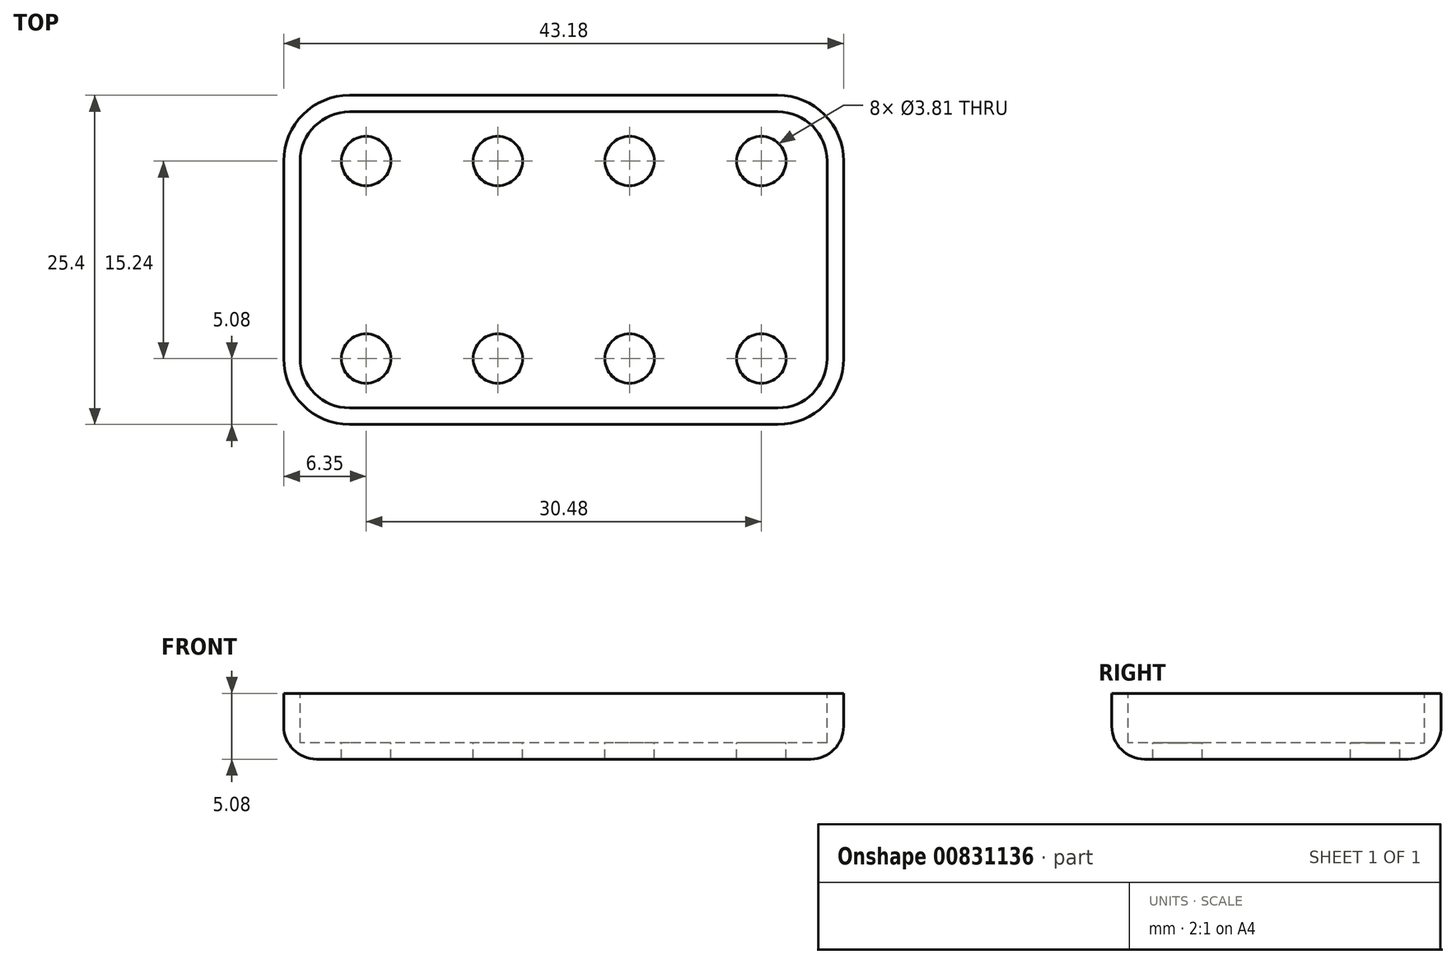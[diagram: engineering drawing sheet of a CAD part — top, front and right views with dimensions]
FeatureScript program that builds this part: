
annotation { "Feature Type Name" : "Feature", "Feature Type Description" : "" }
export const myFeature = defineFeature(function(context is Context, id is Id, definition is map)
    precondition{}
    {
        {
            var Q0;
            Q0=qCreatedBy(makeId("Top.planeOp"),FACE);
            var sketch = newSketch(context, id + "F0", { "sketchPlane" : qUnion([Q0])});
            skLineSegment(sketch, "E0.bottom", {"start": v(-22.86, 12.7) * mm, "end": v(22.86, 12.7) * mm});
            skLineSegment(sketch, "E0.top", {"start": v(-22.86, -12.7) * mm, "end": v(22.86, -12.7) * mm});
            skLineSegment(sketch, "E0.left", {"start": v(-22.86, 12.7) * mm, "end": v(-22.86, -12.7) * mm});
            skLineSegment(sketch, "E0.right", {"start": v(22.86, 12.7) * mm, "end": v(22.86, -12.7) * mm});
            skSolve(sketch);
        }
        {
            var Q0;
            Q0=qCreatedBy(makeId("Top.planeOp"),FACE);
            var sketch = newSketch(context, id + "F1", { "sketchPlane" : qUnion([Q0])});
            skLineSegment(sketch, "E1.bottom", {"start": v(16.51, 12.7) * mm, "end": v(-16.5, 12.7) * mm});
            skLineSegment(sketch, "E1.top", {"start": v(16.51, -12.7) * mm, "end": v(-16.5, -12.7) * mm});
            skLineSegment(sketch, "E1.left", {"start": v(21.6, 7.62) * mm, "end": v(21.6, -7.62) * mm});
            skLineSegment(sketch, "E1.right", {"start": v(-21.59, 7.62) * mm, "end": v(-21.59, -7.62) * mm});
            skPoint(sketch, "E1.middle", {"position": v(0, 0) * mm});
            skPoint(sketch, "E2.visualSharp", {"position": v(-21.59, 12.7) * mm});
            skArc(sketch, "E2.filletArc", {"start": v(-16.5, 12.7) * mm, "mid": v(-20.1, 11.21) * mm, "end": v(-21.59, 7.62) * mm});
            skPoint(sketch, "E3.visualSharp", {"position": v(21.59, 12.7) * mm});
            skArc(sketch, "E3.filletArc", {"start": v(21.59, 7.62) * mm, "mid": v(20.1, 11.21) * mm, "end": v(16.51, 12.7) * mm});
            skPoint(sketch, "E4.visualSharp", {"position": v(21.6, -12.7) * mm});
            skArc(sketch, "E4.filletArc", {"start": v(16.51, -12.7) * mm, "mid": v(20.1, -11.21) * mm, "end": v(21.6, -7.62) * mm});
            skPoint(sketch, "E5.visualSharp", {"position": v(-21.59, -12.7) * mm});
            skArc(sketch, "E5.filletArc", {"start": v(-21.59, -7.62) * mm, "mid": v(-20.1, -11.21) * mm, "end": v(-16.5, -12.7) * mm});
            skSolve(sketch);
        }
        {
            var Q0;
            Q0=qCreatedBy(makeId("Top.planeOp"),FACE);
            cPlane(context, id + "F2", {"entities" : qUnion([Q0]), "cplaneType" : CPlaneType.OFFSET, "offset" : 7.62 * mm, "oppositeDirection" : true, "width" : 152.4 * mm, "height" : 152.4 * mm});
        }
        {
            var Q0;
            Q0=qCreatedBy(id+"F2.planeOp",FACE);
            var sketch = newSketch(context, id + "F3", { "sketchPlane" : qUnion([Q0])});
            skCircle(sketch, "E6", {"center": v(15.24, -7.62) * mm, "radius": 1.52 * mm});
            skCircle(sketch, "E7", {"center": v(15.24, 7.62) * mm, "radius": 1.52 * mm});
            skCircle(sketch, "E8.1.0.0", {"center": v(5.08, -7.62) * mm, "radius": 1.52 * mm});
            skCircle(sketch, "E8.2.0.0", {"center": v(-5.08, -7.62) * mm, "radius": 1.52 * mm});
            skCircle(sketch, "E8.3.0.0", {"center": v(-15.24, -7.62) * mm, "radius": 1.52 * mm});
            skLineSegment(sketch, "E8.direction1", {"start": v(15.24, -7.62) * mm, "end": v(5.08, -7.62) * mm, "construction": true});
            skCircle(sketch, "E9.1.0.0", {"center": v(5.08, 7.62) * mm, "radius": 1.52 * mm});
            skCircle(sketch, "E9.2.0.0", {"center": v(-5.08, 7.62) * mm, "radius": 1.52 * mm});
            skCircle(sketch, "E9.3.0.0", {"center": v(-15.24, 7.62) * mm, "radius": 1.52 * mm});
            skLineSegment(sketch, "E9.direction1", {"start": v(15.24, 7.62) * mm, "end": v(5.08, 7.62) * mm, "construction": true});
            skSolve(sketch);
        }
        {
            var Q0;
            Q0=makeQuery(id+"F1.imprint","IMPRINT",FACE,{"disambiguationData":[TD([[makeQuery(id+"F1.imprint","IMPRINT",EDGE,{"derivedFrom":sQuery(id+"F1.wireOp",EDGE,"E1.bottom")}),1.0]])]});
            extrude(context, id + "F4", {"entities" : qUnion([Q0]), "oppositeDirection" : true, "depth" : 5.08 * mm, "offsetDistance" : 25.4 * mm});
        }
        {
            var Q0;
            Q0=makeQuery(id+"F4.opExtrude","CAP_FACE",FACE,{"disambiguationData":[OSD([sQuery(id+"F1.wireOp",EDGE,"E1.bottom"),sQuery(id+"F1.wireOp",EDGE,"E1.top"),sQuery(id+"F1.wireOp",EDGE,"E1.left"),sQuery(id+"F1.wireOp",EDGE,"E1.right"),sQuery(id+"F1.wireOp",EDGE,"E2.filletArc"),sQuery(id+"F1.wireOp",EDGE,"E3.filletArc"),sQuery(id+"F1.wireOp",EDGE,"E4.filletArc"),sQuery(id+"F1.wireOp",EDGE,"E5.filletArc")])],"isStart":true});
            shell(context, id + "F5", {"entities" : qUnion([Q0]), "thickness" : 1.27 * mm});
        }
        {
            var Q0;
            Q0=qSketchRegion(id+"F3",true);
            extrude(context, id + "F6", {"entities" : qUnion([Q0]), "operationType" : NewBodyOperationType.REMOVE, "oppositeDirection" : true, "depth" : 25.4 * mm, "offsetDistance" : 25.4 * mm});
        }
        {
            var Q0;
            Q0=makeQuery(id+"F0.imprint","IMPRINT",FACE,{"disambiguationData":[TD([[makeQuery(id+"F0.imprint","IMPRINT",EDGE,{"derivedFrom":sQuery(id+"F0.wireOp",EDGE,"E0.bottom")}),-1.0]])]});
            var sketch = newSketch(context, id + "F7", { "sketchPlane" : qUnion([Q0])});
            skCircle(sketch, "E10", {"center": v(15.24, -7.62) * mm, "radius": 1.9 * mm});
            skCircle(sketch, "E11.1.0.0", {"center": v(5.08, -7.62) * mm, "radius": 1.9 * mm});
            skCircle(sketch, "E11.2.0.0", {"center": v(-5.08, -7.62) * mm, "radius": 1.9 * mm});
            skCircle(sketch, "E11.3.0.0", {"center": v(-15.24, -7.62) * mm, "radius": 1.9 * mm});
            skLineSegment(sketch, "E11.direction1", {"start": v(15.24, -7.62) * mm, "end": v(5.08, -7.62) * mm, "construction": true});
            skCircle(sketch, "E12.1.0.0", {"center": v(15.24, 7.62) * mm, "radius": 1.9 * mm});
            skLineSegment(sketch, "E12.direction1", {"start": v(15.24, -7.62) * mm, "end": v(15.24, 7.62) * mm, "construction": true});
            skCircle(sketch, "E13.1.0.0", {"center": v(5.08, 7.62) * mm, "radius": 1.9 * mm});
            skCircle(sketch, "E13.2.0.0", {"center": v(-5.08, 7.62) * mm, "radius": 1.9 * mm});
            skCircle(sketch, "E13.3.0.0", {"center": v(-15.24, 7.62) * mm, "radius": 1.9 * mm});
            skLineSegment(sketch, "E13.direction1", {"start": v(15.24, 7.62) * mm, "end": v(5.08, 7.62) * mm, "construction": true});
            skSolve(sketch);
        }
        {
            var Q0;
            Q0=qSketchRegion(id+"F7",true);
            extrude(context, id + "F8", {"entities" : qUnion([Q0]), "operationType" : NewBodyOperationType.REMOVE, "oppositeDirection" : true, "depth" : 9.9 * mm, "offsetDistance" : 25.4 * mm});
        }
        {
            var Q0;
            Q0=makeQuery(id+"F4.opExtrude","CAP_EDGE",EDGE,{"disambiguationData":[OSD([sQuery(id+"F1.wireOp",EDGE,"E1.top")])],"isStart":false});
            fillet(context, id + "F9", {"entities" : qUnion([Q0]), "radius" : 2.54 * mm, "tangentPropagation" : true, "allowEdgeOverflow" : false});
        }
    });
